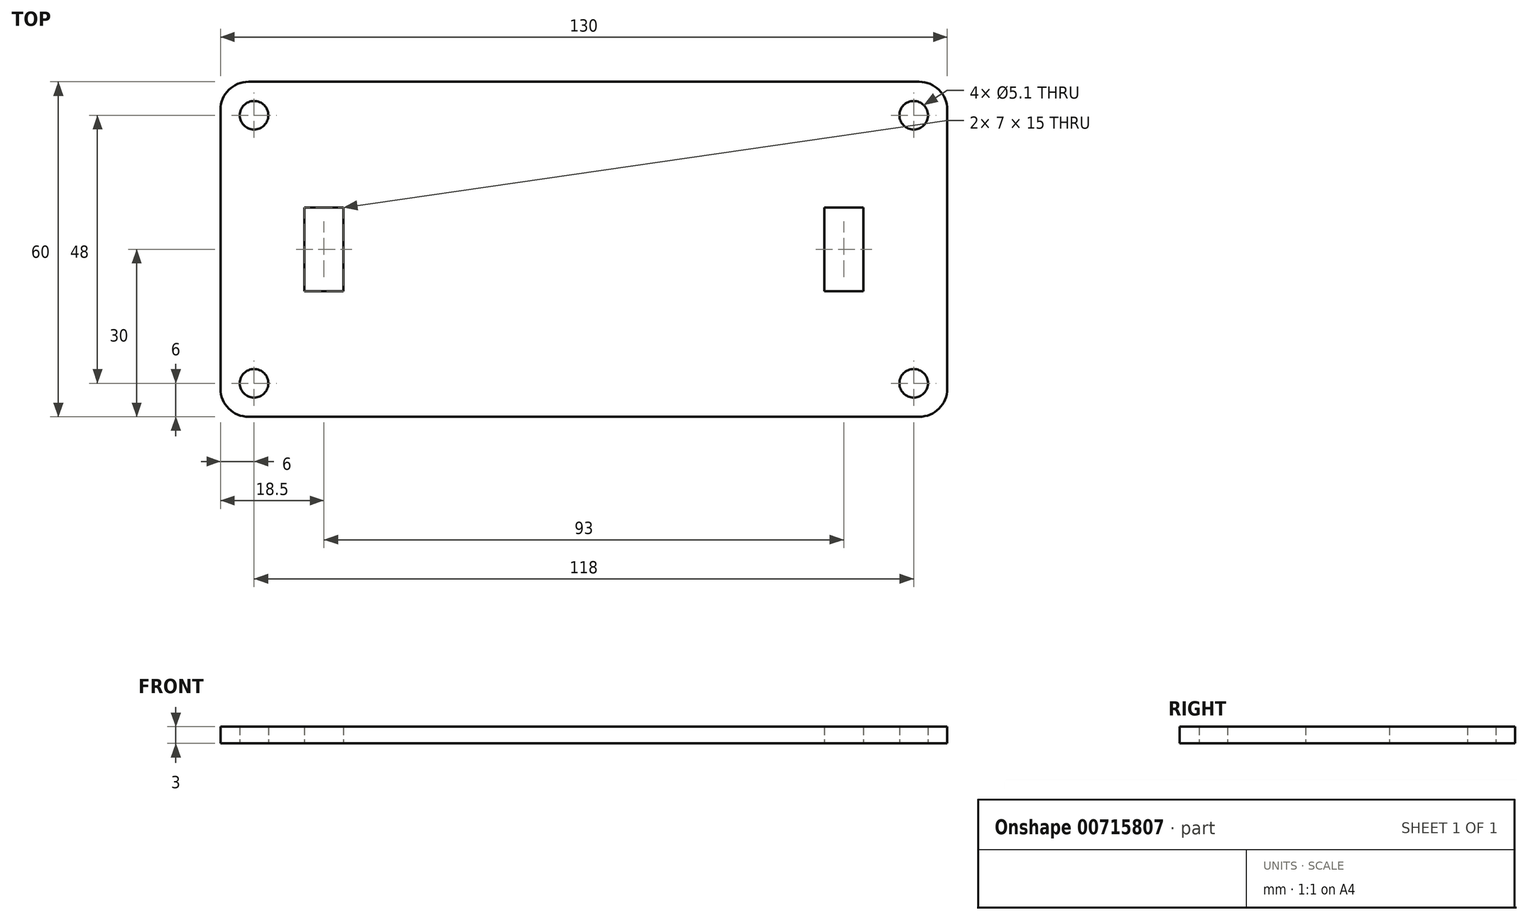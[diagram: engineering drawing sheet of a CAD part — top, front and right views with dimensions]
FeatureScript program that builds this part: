
annotation { "Feature Type Name" : "Feature", "Feature Type Description" : "" }
export const myFeature = defineFeature(function(context is Context, id is Id, definition is map)
    precondition{}
    {
        {
            var Q0;
            Q0=qCreatedBy(makeId("Top.planeOp"),FACE);
            var sketch = newSketch(context, id + "F0", { "sketchPlane" : qUnion([Q0])});
            skLineSegment(sketch, "E0.bottom", {"start": v(0, 0) * mm, "end": v(130, 0) * mm});
            skLineSegment(sketch, "E0.top", {"start": v(0, 60) * mm, "end": v(130, 60) * mm});
            skLineSegment(sketch, "E0.left", {"start": v(0, 0) * mm, "end": v(0, 60) * mm});
            skLineSegment(sketch, "E0.right", {"start": v(130, 0) * mm, "end": v(130, 60) * mm});
            skLineSegment(sketch, "E1", {"start": v(0, 30) * mm, "end": v(130, 30) * mm, "construction": true});
            skLineSegment(sketch, "E2", {"start": v(5, 42.5) * mm, "end": v(5, 30) * mm, "construction": true});
            skLineSegment(sketch, "E3", {"start": v(5, 42.5) * mm, "end": v(0, 42.5) * mm, "construction": true});
            skLineSegment(sketch, "E4", {"start": v(5, 17.5) * mm, "end": v(5, 30) * mm, "construction": true});
            skLineSegment(sketch, "E5", {"start": v(65, 60) * mm, "end": v(65, 0) * mm, "construction": true});
            skLineSegment(sketch, "E6", {"start": v(5, 42.5) * mm, "end": v(15, 42.5) * mm, "construction": true});
            skLineSegment(sketch, "E7", {"start": v(15, 42.5) * mm, "end": v(15, 39.5) * mm, "construction": true});
            skLineSegment(sketch, "E8.bottom", {"start": v(15, 37.5) * mm, "end": v(22, 37.5) * mm});
            skLineSegment(sketch, "E8.top", {"start": v(15, 22.5) * mm, "end": v(22, 22.5) * mm});
            skLineSegment(sketch, "E8.left", {"start": v(15, 37.5) * mm, "end": v(15, 22.5) * mm});
            skLineSegment(sketch, "E8.right", {"start": v(22, 37.5) * mm, "end": v(22, 22.5) * mm});
            skLineSegment(sketch, "E9.MirrorCS", {"start": v(115, 37.5) * mm, "end": v(108, 37.5) * mm});
            skLineSegment(sketch, "E10.MirrorCS", {"start": v(108, 37.5) * mm, "end": v(108, 22.5) * mm});
            skLineSegment(sketch, "E11.MirrorCS", {"start": v(115, 22.5) * mm, "end": v(108, 22.5) * mm});
            skLineSegment(sketch, "E12.MirrorCS", {"start": v(115, 37.5) * mm, "end": v(115, 22.5) * mm});
            skLineSegment(sketch, "E13", {"start": v(6, 54) * mm, "end": v(0, 54) * mm, "construction": true});
            skLineSegment(sketch, "E14", {"start": v(6, 54) * mm, "end": v(6, 60) * mm, "construction": true});
            skCircle(sketch, "E15", {"center": v(6, 54) * mm, "radius": 2.55 * mm});
            skCircle(sketch, "E16.MirrorC", {"center": v(6, 6) * mm, "radius": 2.55 * mm});
            skCircle(sketch, "E17.MirrorC", {"center": v(124, 54) * mm, "radius": 2.55 * mm});
            skCircle(sketch, "E18.MirrorC", {"center": v(124, 6) * mm, "radius": 2.55 * mm});
            skSolve(sketch);
        }
        {
            var Q0;
            Q0=makeQuery(id+"F0.imprint","IMPRINT",FACE,{"disambiguationData":[TD([[makeQuery(id+"F0.imprint","IMPRINT",EDGE,{"derivedFrom":sQuery(id+"F0.wireOp",EDGE,"E0.bottom")}),1.0]])]});
            extrude(context, id + "F1", {"entities" : qUnion([Q0]), "depth" : 3 * mm, "offsetDistance" : 25 * mm});
        }
        {
            var Q0;
            Q0=makeQuery(id+"F1.opExtrude","SWEPT_EDGE",EDGE,{"disambiguationData":[OSD([sQuery(id+"F0.wireOp",EDGE,"E0.bottom"),sQuery(id+"F0.wireOp",EDGE,"E0.right")])]});
            var Q1;
            Q1=makeQuery(id+"F1.opExtrude","SWEPT_EDGE",EDGE,{"disambiguationData":[OSD([sQuery(id+"F0.wireOp",EDGE,"E0.top"),sQuery(id+"F0.wireOp",EDGE,"E0.right")])]});
            var Q2;
            Q2=makeQuery(id+"F1.opExtrude","SWEPT_EDGE",EDGE,{"disambiguationData":[OSD([sQuery(id+"F0.wireOp",EDGE,"E0.bottom"),sQuery(id+"F0.wireOp",EDGE,"E0.left")])]});
            var Q3;
            Q3=makeQuery(id+"F1.opExtrude","SWEPT_EDGE",EDGE,{"disambiguationData":[OSD([sQuery(id+"F0.wireOp",EDGE,"E0.top"),sQuery(id+"F0.wireOp",EDGE,"E0.left")])]});
            fillet(context, id + "F2", {"entities" : qUnion([Q0, Q1, Q2, Q3]), "radius" : 5 * mm, "tangentPropagation" : true, "allowEdgeOverflow" : false});
        }
    });
